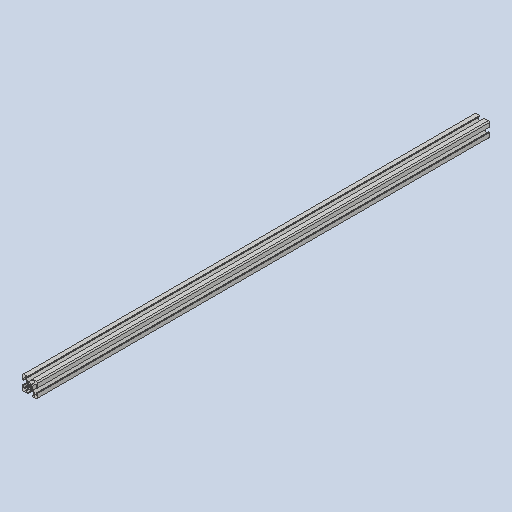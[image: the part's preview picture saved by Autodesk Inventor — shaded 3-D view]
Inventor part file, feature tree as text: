
AUTODESK INVENTOR PART (.ipt)
format: ipt  version: 2023 (Build 270158000, 158)  size: 232,448 bytes
history: native  units: mm
features: plane x2, extrude x1, sketch x1
ambient origin geometry x8: Origin, YZ Plane, XZ Plane, XY Plane, X Axis, Y Axis, Z Axis, Center Point
bodies: Solid1 (feature_tree)
feature tree (4):
  extrude  "Extrusion1"  [1 undecoded]
  plane  "Work Plane1"
  plane  "Work Plane2"
  sketch  "Sketch_1"  dims[d0=600.0mm d1=0.0mm]
note: 1 required parameter value undecoded (feature->parameter linkage not recoverable at this tier; creation-order binding heuristic only, values carry confidence <= 0.55)
